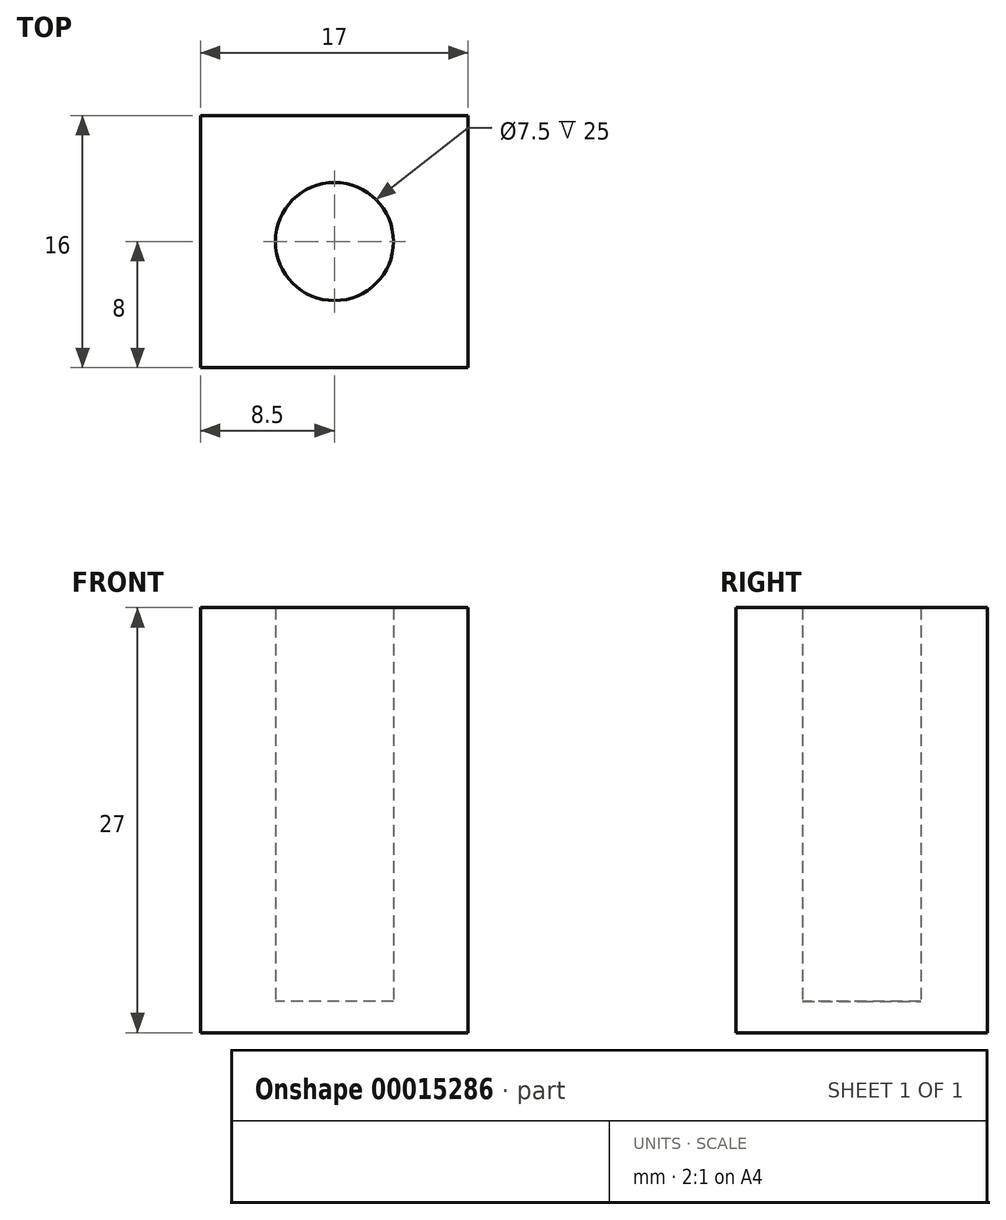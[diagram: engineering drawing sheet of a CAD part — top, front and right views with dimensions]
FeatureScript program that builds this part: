
annotation { "Feature Type Name" : "Feature", "Feature Type Description" : "" }
export const myFeature = defineFeature(function(context is Context, id is Id, definition is map)
    precondition{}
    {
        {
            var Q0;
            Q0=qCreatedBy(makeId("Top.planeOp"),FACE);
            var sketch = newSketch(context, id + "F0", { "sketchPlane" : qUnion([Q0])});
            skLineSegment(sketch, "E0.bottom", {"start": v(0, 0) * mm, "end": v(17, 0) * mm});
            skLineSegment(sketch, "E0.top", {"start": v(0, -16) * mm, "end": v(17, -16) * mm});
            skLineSegment(sketch, "E0.left", {"start": v(0, 0) * mm, "end": v(0, -16) * mm});
            skLineSegment(sketch, "E0.right", {"start": v(17, 0) * mm, "end": v(17, -16) * mm});
            skLineSegment(sketch, "E1", {"start": v(8.5, 0) * mm, "end": v(8.5, -16) * mm, "construction": true});
            skLineSegment(sketch, "E2", {"start": v(8.5, -16) * mm, "end": v(8.5, -8) * mm, "construction": true});
            skCircle(sketch, "E3", {"center": v(8.5, -8) * mm, "radius": 3.75 * mm});
            skSolve(sketch);
        }
        {
            var Q0;
            Q0 = qSketchRegion(id + "F0", true);
            var Q1;
            Q1=makeQuery(id+"F0.imprint","IMPRINT",FACE,{"disambiguationData":[TD([[makeQuery(id+"F0.imprint","IMPRINT",EDGE,{"derivedFrom":sQuery(id+"F0.wireOp",EDGE,"E3")}),1.0]])]});
            extrude(context, id + "F1", {"entities" : qUnion([Q0, Q1]), "oppositeDirection" : true, "depth" : 2 * mm});
        }
        {
            var Q0;
            Q0 = qSketchRegion(id + "F0", true);
            extrude(context, id + "F2", {"entities" : qUnion([Q0]), "operationType" : NewBodyOperationType.ADD, "depth" : 25 * mm});
        }
    });
